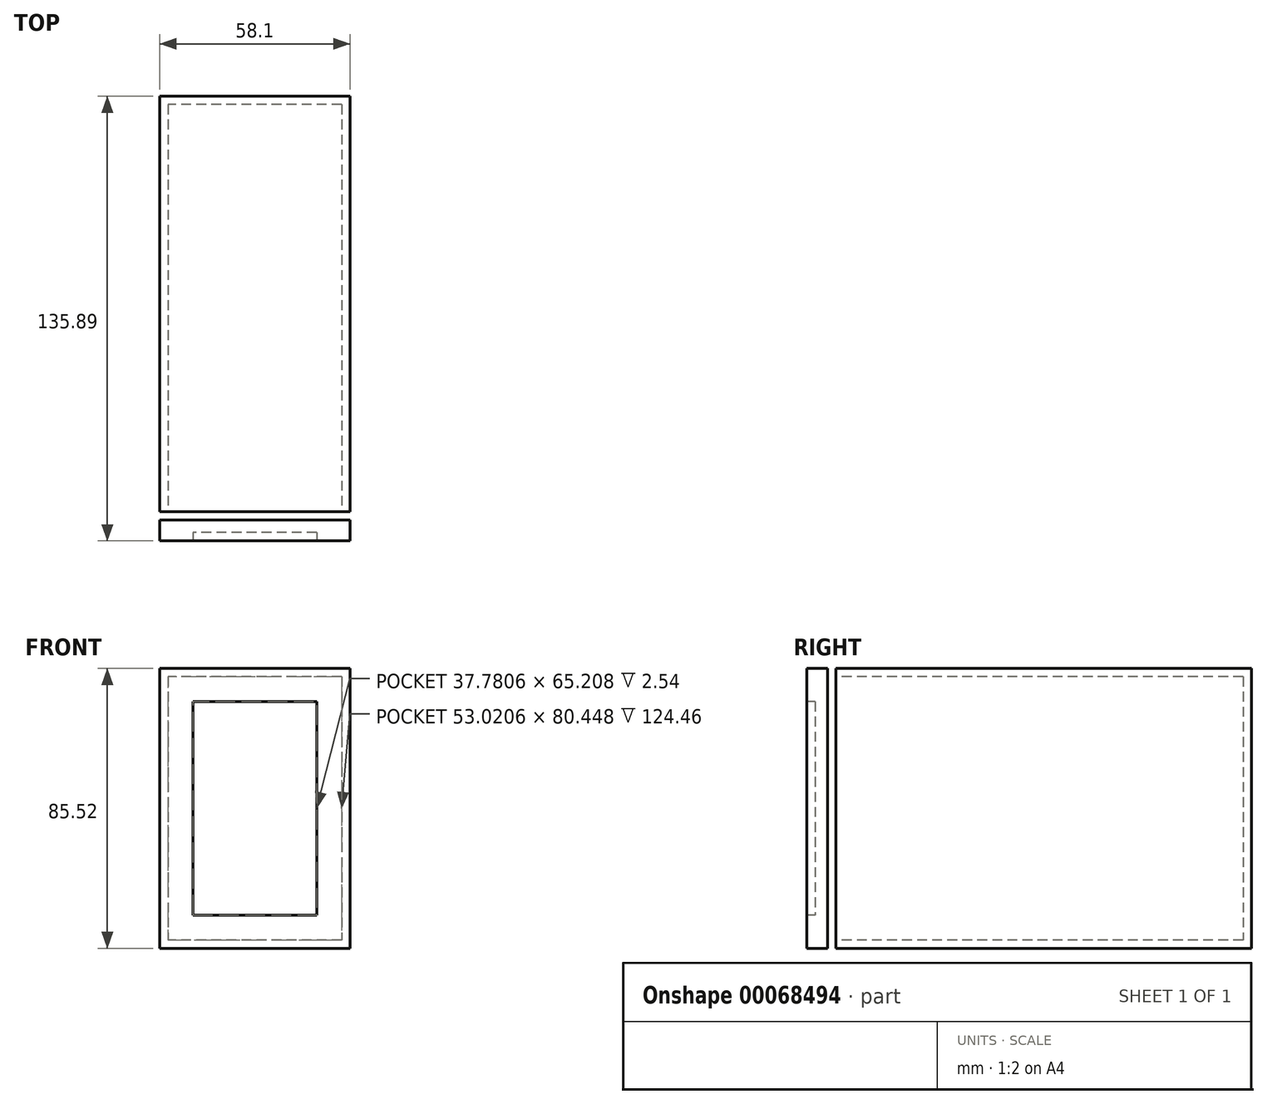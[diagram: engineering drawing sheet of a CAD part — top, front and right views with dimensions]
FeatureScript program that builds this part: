
annotation { "Feature Type Name" : "Feature", "Feature Type Description" : "" }
export const myFeature = defineFeature(function(context is Context, id is Id, definition is map)
    precondition{}
    {
        {
            var Q0;
            Q0=qCreatedBy(makeId("Front.planeOp"),FACE);
            var sketch = newSketch(context, id + "F0", { "sketchPlane" : qUnion([Q0])});
            skLineSegment(sketch, "E0.rect.bottom", {"start": v(29.05, 42.76) * mm, "end": v(-29.05, 42.76) * mm});
            skLineSegment(sketch, "E0.rect.top", {"start": v(29.05, -42.76) * mm, "end": v(-29.05, -42.76) * mm});
            skLineSegment(sketch, "E0.rect.left", {"start": v(29.05, 42.76) * mm, "end": v(29.05, -42.76) * mm});
            skLineSegment(sketch, "E0.rect.right", {"start": v(-29.05, 42.76) * mm, "end": v(-29.05, -42.76) * mm});
            skPoint(sketch, "E0.rect.middle", {"position": v(0, 0) * mm});
            skSolve(sketch);
        }
        {
            var Q0;
            Q0=makeQuery(id+"F0.imprint","IMPRINT",FACE,{"disambiguationData":[TD([[makeQuery(id+"F0.imprint","IMPRINT",EDGE,{"derivedFrom":sQuery(id+"F0.wireOp",EDGE,"E0.rect.bottom")}),1.0]])]});
            extrude(context, id + "F1", {"entities" : qUnion([Q0]), "oppositeDirection" : true, "depth" : 127 * mm});
        }
        {
            var Q0;
            Q0=makeQuery(id+"F1.opExtrude","CAP_FACE",FACE,{"disambiguationData":[OSD([sQuery(id+"F0.wireOp",EDGE,"E0.rect.bottom"),sQuery(id+"F0.wireOp",EDGE,"E0.rect.top"),sQuery(id+"F0.wireOp",EDGE,"E0.rect.left"),sQuery(id+"F0.wireOp",EDGE,"E0.rect.right")])],"isStart":true});
            shell(context, id + "F2", {"entities" : qUnion([Q0]), "thickness" : 2.54 * mm});
        }
        {
            var Q0;
            Q0=qCreatedBy(makeId("Front.planeOp"),FACE);
            var sketch = newSketch(context, id + "F3", { "sketchPlane" : qUnion([Q0])});
            skLineSegment(sketch, "E1.rect.bottom", {"start": v(29.05, 42.76) * mm, "end": v(-29.05, 42.76) * mm});
            skLineSegment(sketch, "E1.rect.top", {"start": v(29.05, -42.76) * mm, "end": v(-29.05, -42.76) * mm});
            skLineSegment(sketch, "E1.rect.left", {"start": v(29.05, 42.76) * mm, "end": v(29.05, -42.76) * mm});
            skLineSegment(sketch, "E1.rect.right", {"start": v(-29.05, 42.76) * mm, "end": v(-29.05, -42.76) * mm});
            skPoint(sketch, "E1.rect.middle", {"position": v(0, 0) * mm});
            skSolve(sketch);
        }
        {
            var Q0;
            Q0 = qSketchRegion(id + "F3", true);
            extrude(context, id + "F4", {"entities" : qUnion([Q0]), "depth" : 6.35 * mm});
        }
        {
            var Q0;
            Q0=makeQuery(id+"F4.opExtrude","SWEPT_BODY",BODY,{"disambiguationData":[OSD([sQuery(id+"F3.wireOp",EDGE,"E1.rect.bottom"),sQuery(id+"F3.wireOp",EDGE,"E1.rect.top"),sQuery(id+"F3.wireOp",EDGE,"E1.rect.left"),sQuery(id+"F3.wireOp",EDGE,"E1.rect.right")])]});
            var Q1;
            Q1=qCreatedBy(makeId("Front.planeOp"),FACE);
            transform(context, id + "F5", {"entities" : qUnion([Q0]), "transformType" : TransformType.TRANSLATION_DISTANCE, "transformDirection" : qUnion([Q1]), "distance" : 2.54 * mm, "makeCopy" : false});
        }
        {
            var Q0;
            Q0=makeQuery(id+"F4.opExtrude","CAP_FACE",FACE,{"disambiguationData":[OSD([sQuery(id+"F3.wireOp",EDGE,"E1.rect.bottom"),sQuery(id+"F3.wireOp",EDGE,"E1.rect.top"),sQuery(id+"F3.wireOp",EDGE,"E1.rect.left"),sQuery(id+"F3.wireOp",EDGE,"E1.rect.right")])],"isStart":false});
            var sketch = newSketch(context, id + "F6", { "sketchPlane" : qUnion([Q0])});
            skLineSegment(sketch, "E2.rect.bottom", {"start": v(18.9, 32.6) * mm, "end": v(-18.9, 32.6) * mm});
            skLineSegment(sketch, "E2.rect.top", {"start": v(18.9, -32.6) * mm, "end": v(-18.9, -32.6) * mm});
            skLineSegment(sketch, "E2.rect.left", {"start": v(18.9, 32.6) * mm, "end": v(18.9, -32.6) * mm});
            skLineSegment(sketch, "E2.rect.right", {"start": v(-18.9, 32.6) * mm, "end": v(-18.9, -32.6) * mm});
            skPoint(sketch, "E2.rect.middle", {"position": v(0, 0) * mm});
            skSolve(sketch);
        }
        {
            var Q0;
            Q0 = qSketchRegion(id + "F6", true);
            extrude(context, id + "F7", {"entities" : qUnion([Q0]), "operationType" : NewBodyOperationType.REMOVE, "oppositeDirection" : true, "depth" : 2.54 * mm});
        }
    });
